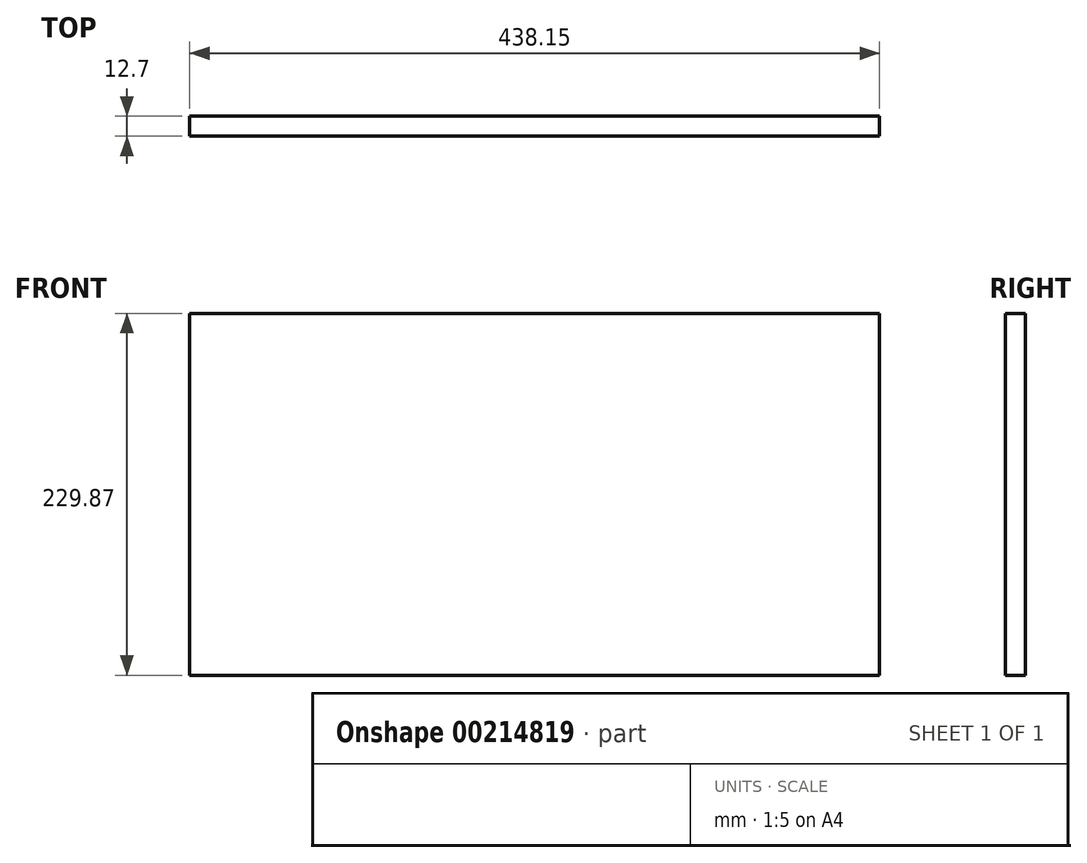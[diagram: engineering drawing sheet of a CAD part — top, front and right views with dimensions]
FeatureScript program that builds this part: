
annotation { "Feature Type Name" : "Feature", "Feature Type Description" : "" }
export const myFeature = defineFeature(function(context is Context, id is Id, definition is map)
    precondition{}
    {
        {
            var Q0;
            Q0=qCreatedBy(makeId("Front.planeOp"),FACE);
            var sketch = newSketch(context, id + "F0", { "sketchPlane" : qUnion([Q0])});
            skLineSegment(sketch, "E0.bottom", {"start": v(0, 0) * mm, "end": v(438.15, 0) * mm});
            skLineSegment(sketch, "E0.top", {"start": v(0, -229.87) * mm, "end": v(438.15, -229.87) * mm});
            skLineSegment(sketch, "E0.left", {"start": v(0, 0) * mm, "end": v(0, -229.87) * mm});
            skLineSegment(sketch, "E0.right", {"start": v(438.15, 0) * mm, "end": v(438.15, -229.87) * mm});
            skSolve(sketch);
        }
        {
            var Q0;
            Q0=makeQuery(id+"F0.imprint","IMPRINT",FACE,{"disambiguationData":[TD([[makeQuery(id+"F0.imprint","IMPRINT",EDGE,{"derivedFrom":sQuery(id+"F0.wireOp",EDGE,"E0.bottom")}),-1.0]])]});
            extrude(context, id + "F1", {"entities" : qUnion([Q0]), "depth" : 12.7 * mm});
        }
    });
